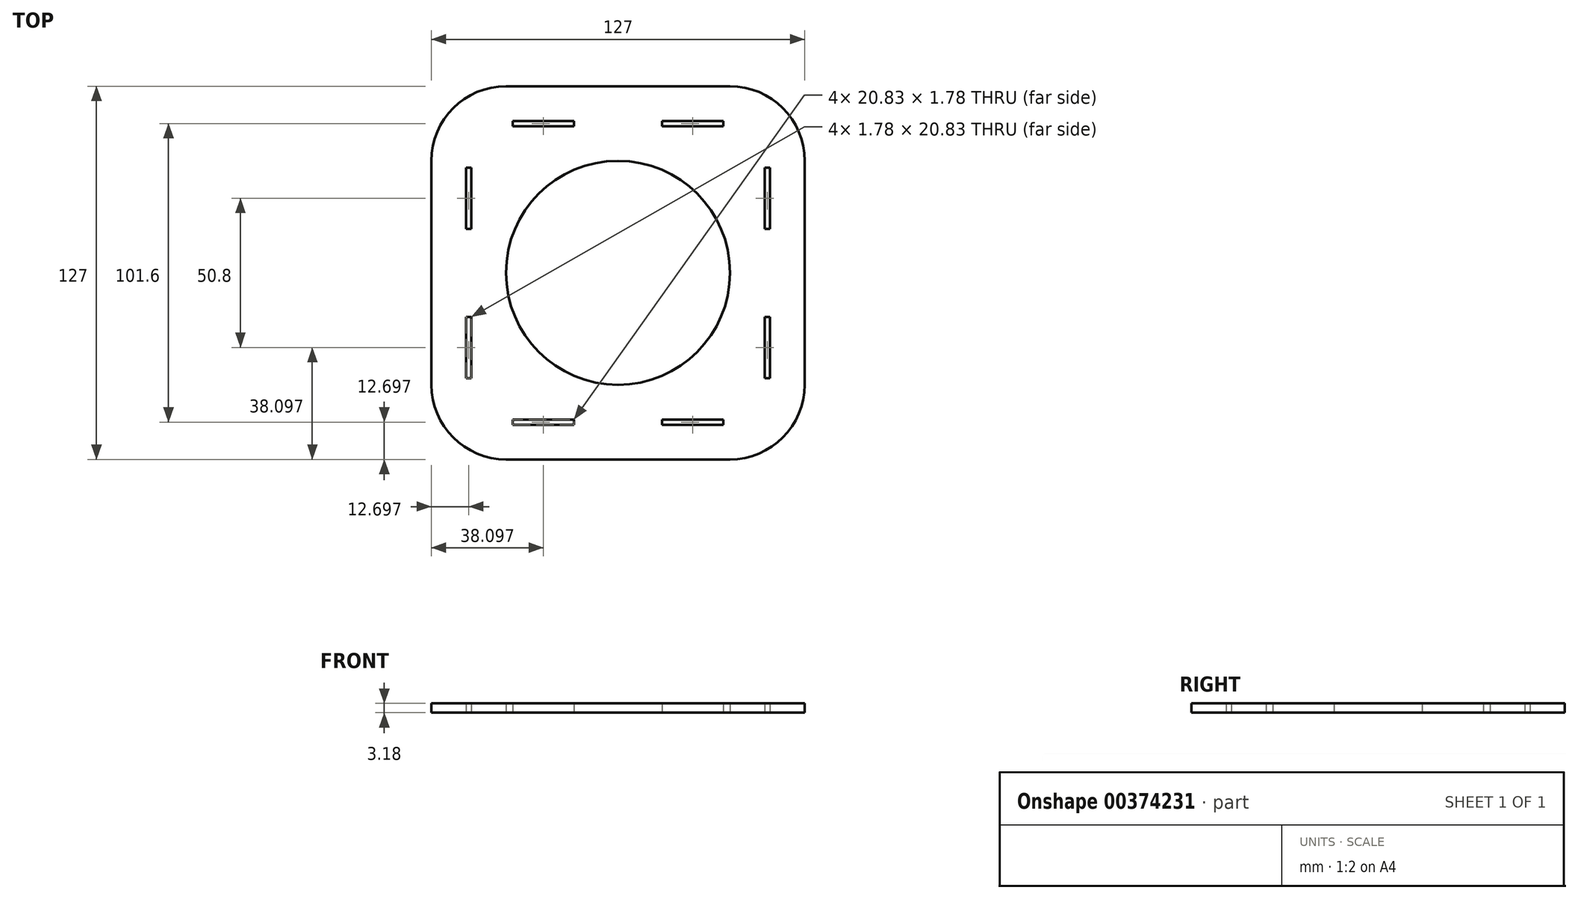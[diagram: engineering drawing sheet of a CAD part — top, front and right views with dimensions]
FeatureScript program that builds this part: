
annotation { "Feature Type Name" : "Feature", "Feature Type Description" : "" }
export const myFeature = defineFeature(function(context is Context, id is Id, definition is map)
    precondition{}
    {
        {
            var Q0;
            Q0=qCreatedBy(makeId("Top.planeOp"),FACE);
            var sketch = newSketch(context, id + "F0", { "sketchPlane" : qUnion([Q0])});
            skLineSegment(sketch, "E0", {"start": v(233.79, -61.91) * mm, "end": v(309.99, -61.91) * mm});
            skLineSegment(sketch, "E1", {"start": v(335.39, -36.51) * mm, "end": v(335.39, 39.69) * mm});
            skLineSegment(sketch, "E2", {"start": v(309.99, 65.09) * mm, "end": v(233.79, 65.09) * mm});
            skLineSegment(sketch, "E3", {"start": v(208.39, 39.69) * mm, "end": v(208.39, -36.51) * mm});
            skLineSegment(sketch, "E4", {"start": v(236.07, 51.5) * mm, "end": v(256.9, 51.5) * mm});
            skLineSegment(sketch, "E5", {"start": v(256.9, 51.5) * mm, "end": v(256.9, 53.28) * mm});
            skLineSegment(sketch, "E6", {"start": v(256.9, 53.28) * mm, "end": v(236.07, 53.28) * mm});
            skLineSegment(sketch, "E7", {"start": v(236.07, 53.28) * mm, "end": v(236.07, 51.5) * mm});
            skLineSegment(sketch, "E8", {"start": v(286.87, 51.5) * mm, "end": v(307.7, 51.5) * mm});
            skLineSegment(sketch, "E9", {"start": v(307.7, 51.5) * mm, "end": v(307.7, 53.28) * mm});
            skLineSegment(sketch, "E10", {"start": v(307.7, 53.28) * mm, "end": v(286.87, 53.28) * mm});
            skLineSegment(sketch, "E11", {"start": v(286.87, 53.28) * mm, "end": v(286.87, 51.5) * mm});
            skLineSegment(sketch, "E12", {"start": v(236.07, -48.32) * mm, "end": v(256.9, -48.32) * mm});
            skLineSegment(sketch, "E13", {"start": v(256.9, -48.32) * mm, "end": v(256.9, -50.1) * mm});
            skLineSegment(sketch, "E14", {"start": v(256.9, -50.1) * mm, "end": v(236.07, -50.1) * mm});
            skLineSegment(sketch, "E15", {"start": v(236.07, -50.1) * mm, "end": v(236.07, -48.32) * mm});
            skLineSegment(sketch, "E16", {"start": v(286.87, -48.32) * mm, "end": v(307.7, -48.32) * mm});
            skLineSegment(sketch, "E17", {"start": v(307.7, -48.32) * mm, "end": v(307.7, -50.1) * mm});
            skLineSegment(sketch, "E18", {"start": v(307.7, -50.1) * mm, "end": v(286.87, -50.1) * mm});
            skLineSegment(sketch, "E19", {"start": v(286.87, -50.1) * mm, "end": v(286.87, -48.32) * mm});
            skLineSegment(sketch, "E20", {"start": v(220.2, -34.23) * mm, "end": v(221.98, -34.23) * mm});
            skLineSegment(sketch, "E21", {"start": v(221.98, -34.23) * mm, "end": v(221.98, -13.4) * mm});
            skLineSegment(sketch, "E22", {"start": v(221.98, -13.4) * mm, "end": v(220.2, -13.4) * mm});
            skLineSegment(sketch, "E23", {"start": v(220.2, -13.4) * mm, "end": v(220.2, -34.23) * mm});
            skLineSegment(sketch, "E24", {"start": v(220.2, 37.4) * mm, "end": v(221.98, 37.4) * mm});
            skLineSegment(sketch, "E25", {"start": v(221.98, 37.4) * mm, "end": v(221.98, 16.57) * mm});
            skLineSegment(sketch, "E26", {"start": v(221.98, 16.57) * mm, "end": v(220.2, 16.57) * mm});
            skLineSegment(sketch, "E27", {"start": v(220.2, 16.57) * mm, "end": v(220.2, 37.4) * mm});
            skLineSegment(sketch, "E28", {"start": v(323.58, -34.23) * mm, "end": v(321.8, -34.23) * mm});
            skLineSegment(sketch, "E29", {"start": v(321.8, -34.23) * mm, "end": v(321.8, -13.4) * mm});
            skLineSegment(sketch, "E30", {"start": v(321.8, -13.4) * mm, "end": v(323.58, -13.4) * mm});
            skLineSegment(sketch, "E31", {"start": v(323.58, -13.4) * mm, "end": v(323.58, -34.23) * mm});
            skLineSegment(sketch, "E32", {"start": v(323.58, 37.4) * mm, "end": v(321.8, 37.4) * mm});
            skLineSegment(sketch, "E33", {"start": v(321.8, 37.4) * mm, "end": v(321.8, 16.57) * mm});
            skLineSegment(sketch, "E34", {"start": v(321.8, 16.57) * mm, "end": v(323.58, 16.57) * mm});
            skLineSegment(sketch, "E35", {"start": v(323.58, 16.57) * mm, "end": v(323.58, 37.4) * mm});
            skArc(sketch, "E36", {"start": v(233.79, 65.09) * mm, "mid": v(215.83, 57.65) * mm, "end": v(208.39, 39.69) * mm});
            skArc(sketch, "E37", {"start": v(335.39, 39.69) * mm, "mid": v(327.95, 57.65) * mm, "end": v(309.99, 65.09) * mm});
            skArc(sketch, "E38", {"start": v(309.99, -61.91) * mm, "mid": v(327.95, -54.47) * mm, "end": v(335.39, -36.51) * mm});
            skArc(sketch, "E39", {"start": v(208.39, -36.51) * mm, "mid": v(215.83, -54.47) * mm, "end": v(233.79, -61.91) * mm});
            skCircle(sketch, "E40", {"center": v(271.89, 1.59) * mm, "radius": 38.1 * mm});
            skSolve(sketch);
        }
        {
            var Q0;
            Q0=makeQuery(id+"F0.imprint","IMPRINT",FACE,{"disambiguationData":[TD([[makeQuery(id+"F0.imprint","IMPRINT",EDGE,{"derivedFrom":sQuery(id+"F0.wireOp",EDGE,"E0")}),1.0]])]});
            extrude(context, id + "F1", {"entities" : qUnion([Q0]), "depth" : 3.17 * mm});
        }
    });
